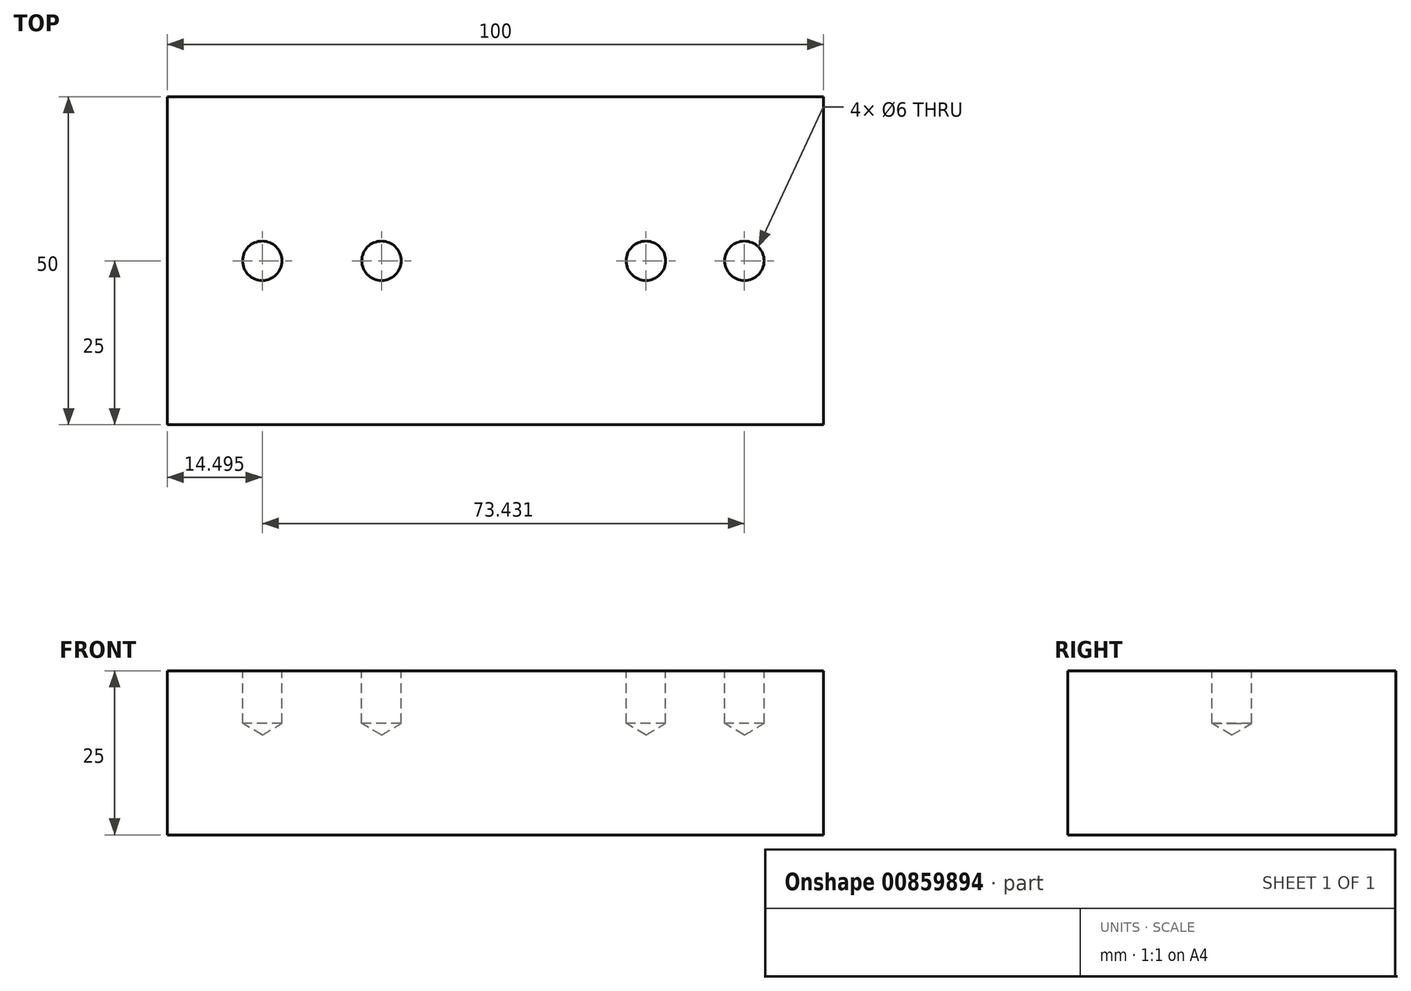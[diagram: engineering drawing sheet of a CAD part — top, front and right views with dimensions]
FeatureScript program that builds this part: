
annotation { "Feature Type Name" : "Feature", "Feature Type Description" : "" }
export const myFeature = defineFeature(function(context is Context, id is Id, definition is map)
    precondition{}
    {
        {
            var Q0;
            Q0=qCreatedBy(makeId("Top.planeOp"),FACE);
            var sketch = newSketch(context, id + "F0", { "sketchPlane" : qUnion([Q0])});
            skLineSegment(sketch, "E0.bottom", {"start": v(-50, 25) * mm, "end": v(50, 25) * mm});
            skLineSegment(sketch, "E0.top", {"start": v(-50, -25) * mm, "end": v(50, -25) * mm});
            skLineSegment(sketch, "E0.left", {"start": v(-50, 25) * mm, "end": v(-50, -25) * mm});
            skLineSegment(sketch, "E0.right", {"start": v(50, 25) * mm, "end": v(50, -25) * mm});
            skSolve(sketch);
        }
        {
            var Q0;
            Q0 = qSketchRegion(id + "F0", true);
            extrude(context, id + "F1", {"entities" : qUnion([Q0]), "depth" : 25 * mm, "offsetDistance" : 25 * mm});
        }
        {
            var Q0;
            Q0=makeQuery(id+"F1.opExtrude","CAP_FACE",FACE,{"disambiguationData":[OSD([sQuery(id+"F0.wireOp",EDGE,"E0.bottom"),sQuery(id+"F0.wireOp",EDGE,"E0.top"),sQuery(id+"F0.wireOp",EDGE,"E0.left"),sQuery(id+"F0.wireOp",EDGE,"E0.right")])],"isStart":false});
            var sketch = newSketch(context, id + "F2", { "sketchPlane" : qUnion([Q0])});
            skPoint(sketch, "E1", {"position": v(-35.5, 0) * mm});
            skPoint(sketch, "E2", {"position": v(-17.35, 0) * mm});
            skPoint(sketch, "E3", {"position": v(22.93, 0) * mm});
            skPoint(sketch, "E4", {"position": v(37.93, 0) * mm});
            skSolve(sketch);
        }
        {
            var Q0;
            Q0=sQuery(id+"F2.wireOp",VERTEX,"E1");
            var Q1;
            Q1=sQuery(id+"F2.wireOp",VERTEX,"E2");
            var Q2;
            Q2=sQuery(id+"F2.wireOp",VERTEX,"E3");
            var Q3;
            Q3=sQuery(id+"F2.wireOp",VERTEX,"E4");
            var Q4;
            Q4=makeQuery(id+"F1.opExtrude","SWEPT_BODY",BODY,{"disambiguationData":[OSD([sQuery(id+"F0.wireOp",EDGE,"E0.bottom"),sQuery(id+"F0.wireOp",EDGE,"E0.top"),sQuery(id+"F0.wireOp",EDGE,"E0.left"),sQuery(id+"F0.wireOp",EDGE,"E0.right")])]});
            hole(context, id + "F3", {"style" : HoleStyle.SIMPLE, "endStyle" : HoleEndStyle.BLIND, "holeDiameter" : 6 * mm, "majorDiameter" : 5 * mm, "holeDepth" : 8 * mm, "isTappedThrough" : true, "tappedDepth" : 11.5 * mm, "tapClearance" : 3, "locations" : qUnion([Q0, Q1, Q2, Q3]), "scope" : qUnion([Q4])});
        }
    });
